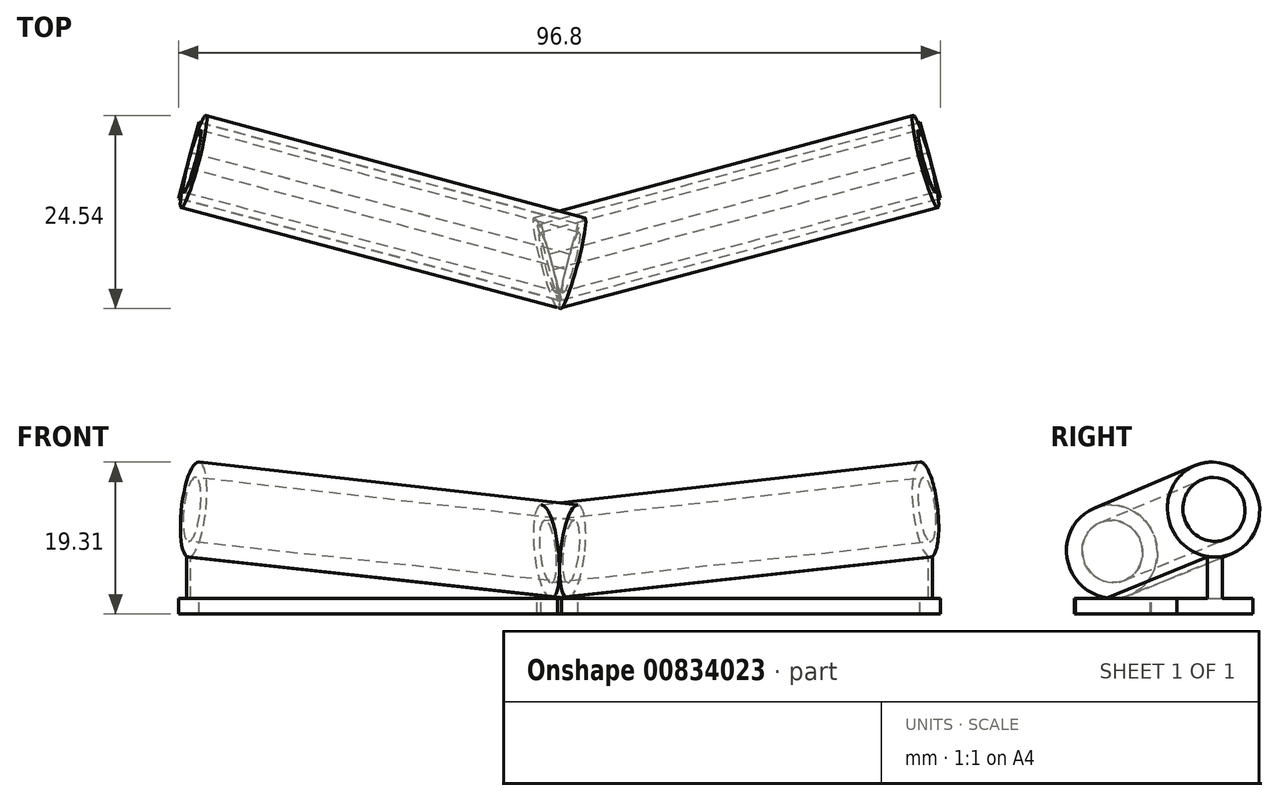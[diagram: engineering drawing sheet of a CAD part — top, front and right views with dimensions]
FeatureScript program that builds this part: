
annotation { "Feature Type Name" : "Feature", "Feature Type Description" : "" }
export const myFeature = defineFeature(function(context is Context, id is Id, definition is map)
    precondition{}
    {
        {
            var Q0;
            Q0=qCreatedBy(makeId("Front.planeOp"),FACE);
            var sketch = newSketch(context, id + "F0", { "sketchPlane" : qUnion([Q0])});
            skLineSegment(sketch, "E0", {"start": v(0, 16.98) * mm, "end": v(0, -4.1) * mm});
            skSolve(sketch);
        }
        {
            var Q0;
            Q0=qCreatedBy(makeId("Right.planeOp"),FACE);
            var Q1;
            Q1=sQuery(id+"F0.wireOp",EDGE,"E0");
            cPlane(context, id + "F1", {"entities" : qUnion([Q0, Q1]), "cplaneType" : CPlaneType.LINE_ANGLE, "offset" : 25 * mm, "angle" : 75 * degree, "width" : 150 * mm, "height" : 150 * mm});
        }
        {
            var Q0;
            Q0=qCreatedBy(id+"F1.planeOp",FACE);
            var sketch = newSketch(context, id + "F2", { "sketchPlane" : qUnion([Q0])});
            skLineSegment(sketch, "E1", {"start": v(1.09, 2) * mm, "end": v(1.09, 4) * mm});
            skLineSegment(sketch, "E2", {"start": v(1.09, 4) * mm, "end": v(1.09, 8) * mm});
            skLineSegment(sketch, "E3", {"start": v(1.09, 0) * mm, "end": v(1.09, 2) * mm});
            skLineSegment(sketch, "E4", {"start": v(0.39, 0) * mm, "end": v(50.25, 0) * mm});
            skLineSegment(sketch, "E5.MirrorCS", {"start": v(1.09, 8) * mm, "end": v(-48.68, 13.33) * mm});
            skLineSegment(sketch, "E6.MirrorCS", {"start": v(-48.78, 10.24) * mm, "end": v(-48.78, 14.24) * mm});
            skLineSegment(sketch, "E7.MirrorCS", {"start": v(1.09, 2) * mm, "end": v(-48.78, 7.24) * mm});
            skLineSegment(sketch, "E8.MirrorCS", {"start": v(1.09, 4) * mm, "end": v(-48.78, 9.24) * mm});
            skLineSegment(sketch, "E9.MirrorCS", {"start": v(-48.78, 3) * mm, "end": v(-48.78, 8.24) * mm});
            skLineSegment(sketch, "E10.MirrorCS", {"start": v(1.09, 0) * mm, "end": v(-48.78, 0) * mm});
            skLineSegment(sketch, "E11.MirrorCS", {"start": v(1.09, 2) * mm, "end": v(-48.78, 2) * mm});
            skLineSegment(sketch, "E12.MirrorCS", {"start": v(-48.78, 0) * mm, "end": v(-48.78, 3) * mm});
            skLineSegment(sketch, "E13.MirrorCS", {"start": v(-48.78, 8.24) * mm, "end": v(-48.78, 10.24) * mm});
            skSolve(sketch);
        }
        {
            var Q0;
            Q0=makeQuery(id+"F2.imprint","IMPRINT",FACE,{"disambiguationData":[TD([[makeQuery(id+"F2.imprint","IMPRINT",EDGE,{"derivedFrom":sQuery(id+"F2.wireOp",EDGE,"E7.MirrorCS")}),1.0]])]});
            extrude(context, id + "F3", {"entities" : qUnion([Q0]), "endBound" : BoundingType.SYMMETRIC, "depth" : 2 * mm, "offsetDistance" : 25 * mm});
        }
        {
            var Q0;
            {var subQ0=sQuery(id+"F2.wireOp",EDGE,"E3");Q0=makeQuery(id+"F2.imprint","IMPRINT",FACE,{"disambiguationData":[TD([[makeQuery(id+"F2.imprint","IMPRINT",EDGE,{"derivedFrom":subQ0}),1.0]])]});}
            extrude(context, id + "F4", {"entities" : qUnion([Q0]), "operationType" : NewBodyOperationType.ADD, "endBound" : BoundingType.SYMMETRIC, "depth" : 10 * mm, "offsetDistance" : 25 * mm});
        }
        {
            var Q0;
            {var subQ0=sQuery(id+"F2.wireOp",EDGE,"E8.MirrorCS");Q0=makeQuery(id+"F2.imprint","IMPRINT",FACE,{"disambiguationData":[TD([[makeQuery(id+"F2.imprint","IMPRINT",EDGE,{"derivedFrom":subQ0}),1.0]])]});}
            var Q1;
            {var subQ0=sQuery(id+"F2.wireOp",EDGE,"E7.MirrorCS");Q1=makeQuery(id+"F2.imprint","IMPRINT",FACE,{"disambiguationData":[TD([[makeQuery(id+"F2.imprint","IMPRINT",EDGE,{"derivedFrom":subQ0}),-1.0]])]});}
            var Q2;
            Q2=sQuery(id+"F2.wireOp",EDGE,"E5.MirrorCS");
            revolve(context, id + "F5", {"operationType" : NewBodyOperationType.ADD, "surfaceOperationType" : NewSurfaceOperationType.NEW, "entities" : qUnion([Q0, Q1]), "axis" : qUnion([Q2]), "revolveType" : RevolveType.FULL});
        }
        {
            var Q0;
            Q0=qCreatedBy(makeId("Right.planeOp"),FACE);
            var Q1;
            Q1=sQuery(id+"F0.wireOp",EDGE,"E0");
            cPlane(context, id + "F6", {"entities" : qUnion([Q0, Q1]), "cplaneType" : CPlaneType.LINE_ANGLE, "offset" : 25 * mm, "angle" : 75 * degree, "oppositeDirection" : true, "width" : 150 * mm, "height" : 150 * mm});
        }
        {
            var Q0;
            Q0=qCreatedBy(id+"F6.planeOp",FACE);
            var sketch = newSketch(context, id + "F7", { "sketchPlane" : qUnion([Q0])});
            skLineSegment(sketch, "E14", {"start": v(1.1, 2) * mm, "end": v(1.1, 4) * mm});
            skLineSegment(sketch, "E15", {"start": v(1.1, 4) * mm, "end": v(1.1, 8) * mm});
            skLineSegment(sketch, "E16", {"start": v(1.1, 0) * mm, "end": v(1.1, 2) * mm});
            skLineSegment(sketch, "E17", {"start": v(-0.2, 0) * mm, "end": v(49.67, 0) * mm});
            skLineSegment(sketch, "E18.MirrorCS", {"start": v(1.1, 8) * mm, "end": v(-48.66, 13.33) * mm});
            skLineSegment(sketch, "E19.MirrorCS", {"start": v(-48.75, 10.24) * mm, "end": v(-48.75, 14.24) * mm});
            skLineSegment(sketch, "E20.MirrorCS", {"start": v(1.1, 2) * mm, "end": v(-48.75, 7.24) * mm});
            skLineSegment(sketch, "E21.MirrorCS", {"start": v(1.1, 4) * mm, "end": v(-48.75, 9.24) * mm});
            skLineSegment(sketch, "E22.MirrorCS", {"start": v(-48.75, 3) * mm, "end": v(-48.75, 8.24) * mm});
            skLineSegment(sketch, "E23.MirrorCS", {"start": v(1.1, 0) * mm, "end": v(-48.75, 0) * mm});
            skLineSegment(sketch, "E24.MirrorCS", {"start": v(1.1, 2) * mm, "end": v(-48.75, 2) * mm});
            skLineSegment(sketch, "E25.MirrorCS", {"start": v(-48.75, 0) * mm, "end": v(-48.75, 2) * mm});
            skLineSegment(sketch, "E26.MirrorCS", {"start": v(-48.75, 8.24) * mm, "end": v(-48.75, 10.24) * mm});
            skLineSegment(sketch, "E27", {"start": v(-48.75, 2) * mm, "end": v(-48.75, 3) * mm});
            skSolve(sketch);
        }
        {
            var Q0;
            Q0=makeQuery(id+"F7.imprint","IMPRINT",FACE,{"disambiguationData":[TD([[makeQuery(id+"F7.imprint","IMPRINT",EDGE,{"derivedFrom":sQuery(id+"F7.wireOp",EDGE,"E20.MirrorCS")}),1.0]])]});
            extrude(context, id + "F8", {"entities" : qUnion([Q0]), "endBound" : BoundingType.SYMMETRIC, "depth" : 2 * mm, "offsetDistance" : 25 * mm});
        }
        {
            var Q0;
            {var subQ0=sQuery(id+"F7.wireOp",EDGE,"E16");Q0=makeQuery(id+"F7.imprint","IMPRINT",FACE,{"disambiguationData":[TD([[makeQuery(id+"F7.imprint","IMPRINT",EDGE,{"derivedFrom":subQ0}),1.0]])]});}
            extrude(context, id + "F9", {"entities" : qUnion([Q0]), "endBound" : BoundingType.SYMMETRIC, "depth" : 10 * mm, "offsetDistance" : 25 * mm});
        }
        {
            var Q0;
            Q0=makeQuery(id+"F7.imprint","IMPRINT",FACE,{"disambiguationData":[TD([[makeQuery(id+"F7.imprint","IMPRINT",EDGE,{"derivedFrom":sQuery(id+"F7.wireOp",EDGE,"E14")}),1.0]])]});
            var Q1;
            Q1=sQuery(id+"F7.wireOp",EDGE,"E18.MirrorCS");
            revolve(context, id + "F10", {"surfaceOperationType" : NewSurfaceOperationType.NEW, "entities" : qUnion([Q0]), "axis" : qUnion([Q1]), "revolveType" : RevolveType.FULL});
        }
        {
            var Q0;
            Q0=makeQuery(id+"F4.opExtrude","SWEPT_FACE",FACE,{"disambiguationData":[OSD([sQuery(id+"F2.wireOp",EDGE,"E3")])]});
            extrude(context, id + "F11", {"entities" : qUnion([Q0]), "depth" : .5 * mm, "offsetDistance" : 25 * mm});
        }
    });
